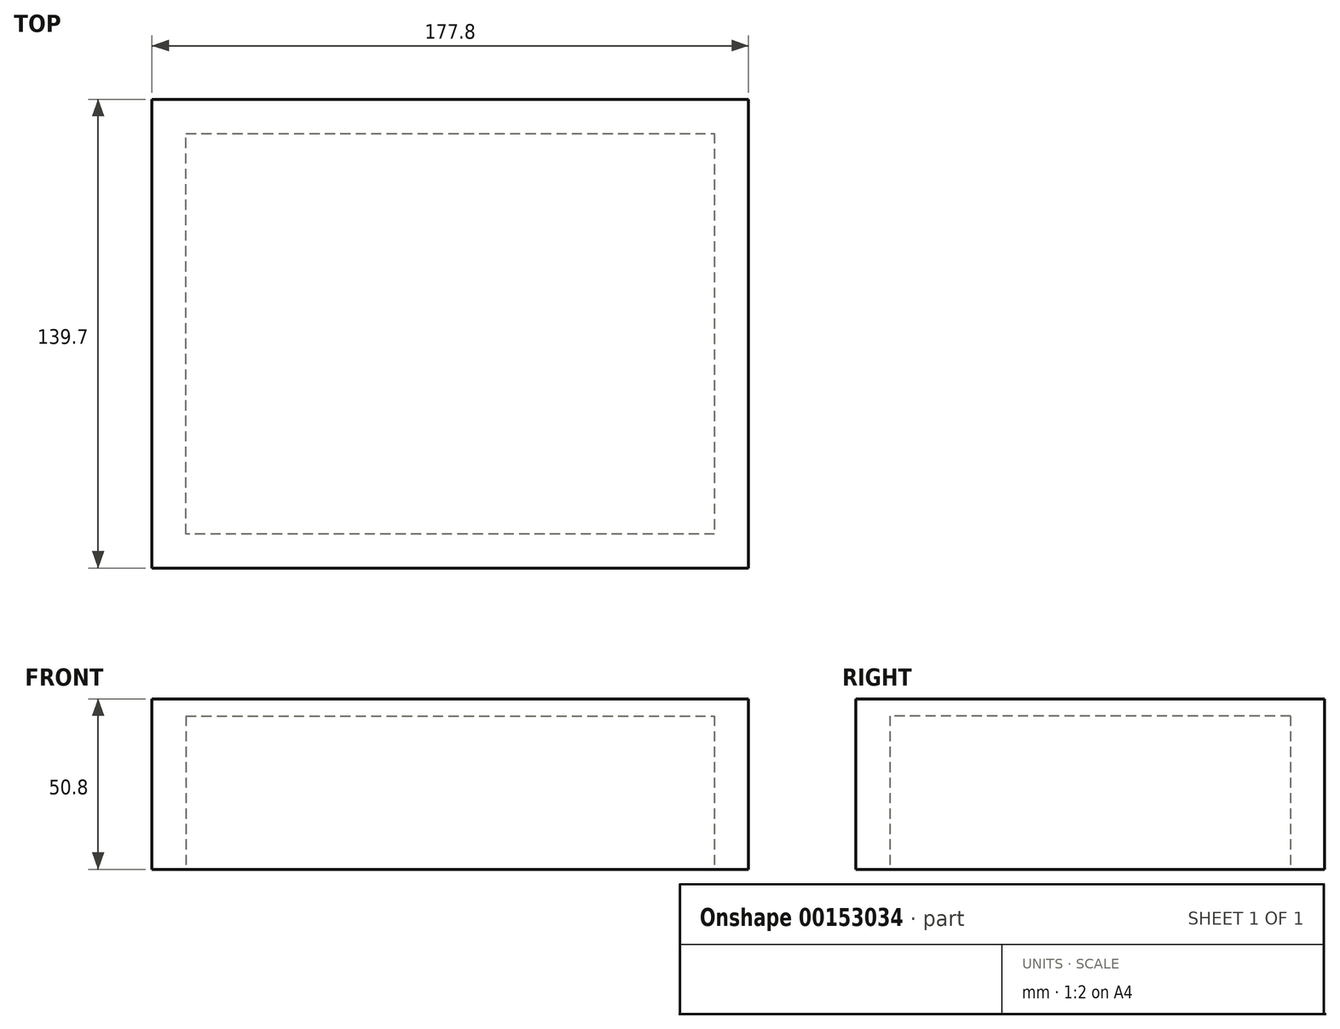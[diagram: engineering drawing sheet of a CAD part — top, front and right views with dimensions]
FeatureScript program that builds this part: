
annotation { "Feature Type Name" : "Feature", "Feature Type Description" : "" }
export const myFeature = defineFeature(function(context is Context, id is Id, definition is map)
    precondition{}
    {
        {
            var Q0;
            Q0=qCreatedBy(makeId("Top.planeOp"),FACE);
            var sketch = newSketch(context, id + "F0", { "sketchPlane" : qUnion([Q0])});
            skLineSegment(sketch, "E0.bottom", {"start": v(88.9, 69.85) * mm, "end": v(-88.9, 69.85) * mm});
            skLineSegment(sketch, "E0.top", {"start": v(88.9, -69.85) * mm, "end": v(-88.9, -69.85) * mm});
            skLineSegment(sketch, "E0.left", {"start": v(88.9, 69.85) * mm, "end": v(88.9, -69.85) * mm});
            skLineSegment(sketch, "E0.right", {"start": v(-88.9, 69.85) * mm, "end": v(-88.9, -69.85) * mm});
            skPoint(sketch, "E0.middle", {"position": v(0, 0) * mm});
            skSolve(sketch);
        }
        {
            var Q0;
            Q0=makeQuery(id+"F0.imprint","IMPRINT",FACE,{"disambiguationData":[TD([[makeQuery(id+"F0.imprint","IMPRINT",EDGE,{"derivedFrom":sQuery(id+"F0.wireOp",EDGE,"E0.bottom")}),1.0]])]});
            extrude(context, id + "F1", {"entities" : qUnion([Q0]), "depth" : 50.8 * mm});
        }
        {
            var Q0;
            Q0=makeQuery(id+"F1.opExtrude","CAP_FACE",FACE,{"disambiguationData":[OSD([sQuery(id+"F0.wireOp",EDGE,"E0.bottom"),sQuery(id+"F0.wireOp",EDGE,"E0.top"),sQuery(id+"F0.wireOp",EDGE,"E0.left"),sQuery(id+"F0.wireOp",EDGE,"E0.right")])],"isStart":true});
            var sketch = newSketch(context, id + "F2", { "sketchPlane" : qUnion([Q0])});
            skLineSegment(sketch, "E1.0", {"start": v(78.74, -59.7) * mm, "end": v(78.74, 59.7) * mm});
            skLineSegment(sketch, "E1.1", {"start": v(-78.74, -59.7) * mm, "end": v(78.74, -59.7) * mm});
            skLineSegment(sketch, "E1.2", {"start": v(-78.74, 59.7) * mm, "end": v(-78.74, -59.7) * mm});
            skLineSegment(sketch, "E1.3", {"start": v(78.74, 59.7) * mm, "end": v(-78.74, 59.7) * mm});
            skSolve(sketch);
        }
        {
            var Q0;
            Q0 = qSketchRegion(id + "F2", true);
            extrude(context, id + "F3", {"entities" : qUnion([Q0]), "operationType" : NewBodyOperationType.REMOVE, "oppositeDirection" : true, "depth" : 45.72 * mm});
        }
    });
